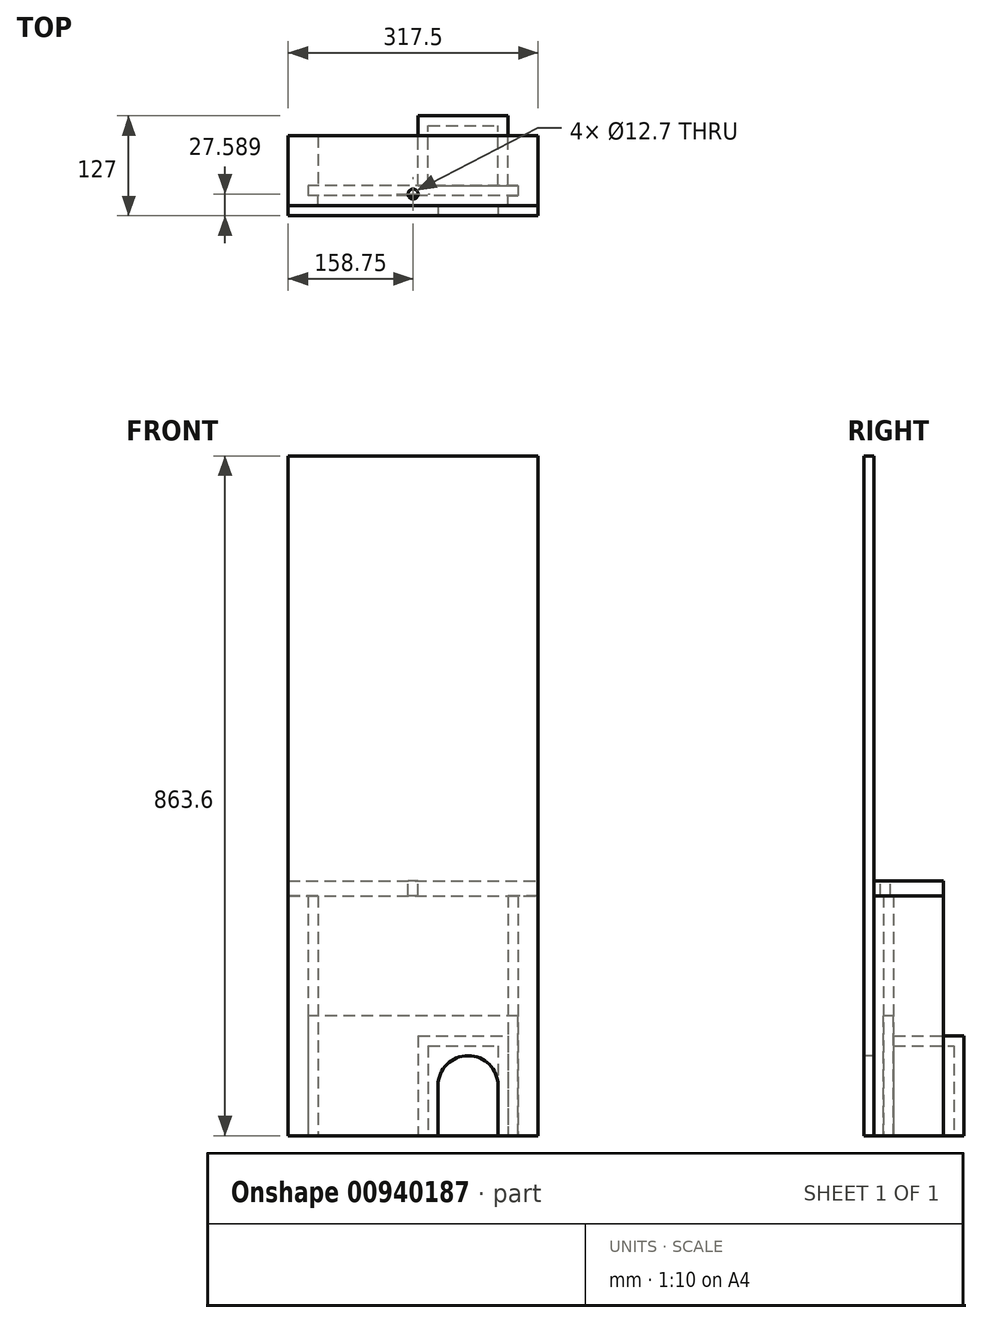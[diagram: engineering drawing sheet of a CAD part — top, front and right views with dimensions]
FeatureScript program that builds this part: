
annotation { "Feature Type Name" : "Feature", "Feature Type Description" : "" }
export const myFeature = defineFeature(function(context is Context, id is Id, definition is map)
    precondition{}
    {
        {
            var Q0;
            Q0=qCreatedBy(makeId("Front.planeOp"),FACE);
            var sketch = newSketch(context, id + "F0", { "sketchPlane" : qUnion([Q0])});
            skLineSegment(sketch, "E0.bottom", {"start": v(158.75, -431.8) * mm, "end": v(-158.75, -431.8) * mm});
            skLineSegment(sketch, "E0.top", {"start": v(158.75, 431.8) * mm, "end": v(-158.75, 431.8) * mm});
            skLineSegment(sketch, "E0.left", {"start": v(158.75, -431.8) * mm, "end": v(158.75, 431.8) * mm});
            skLineSegment(sketch, "E0.right", {"start": v(-158.75, -431.8) * mm, "end": v(-158.75, 431.8) * mm});
            skPoint(sketch, "E0.middle", {"position": v(0, 0) * mm});
            skSolve(sketch);
        }
        {
            var Q0;
            Q0 = qSketchRegion(id + "F0", true);
            extrude(context, id + "F1", {"entities" : qUnion([Q0]), "depth" : 12.7 * mm, "offsetDistance" : 25.4 * mm});
        }
        {
            var Q0;
            Q0=makeQuery(id+"F1.opExtrude","SWEPT_FACE",FACE,{"disambiguationData":[OSD([sQuery(id+"F0.wireOp",EDGE,"E0.bottom")])]});
            var sketch = newSketch(context, id + "F2", { "sketchPlane" : qUnion([Q0])});
            skLineSegment(sketch, "E1", {"start": v(-158.75, 0) * mm, "end": v(-158.75, -88.9) * mm});
            skLineSegment(sketch, "E2", {"start": v(-158.75, -88.9) * mm, "end": v(-120.65, -88.9) * mm});
            skLineSegment(sketch, "E3", {"start": v(-120.65, -88.9) * mm, "end": v(-120.65, -25.4) * mm});
            skLineSegment(sketch, "E4", {"start": v(-120.65, -25.4) * mm, "end": v(-133.35, -25.4) * mm});
            skLineSegment(sketch, "E5", {"start": v(-158.75, 0) * mm, "end": v(-120.65, 0) * mm});
            skLineSegment(sketch, "E6", {"start": v(-120.65, 0) * mm, "end": v(-120.65, -12.7) * mm});
            skLineSegment(sketch, "E7", {"start": v(-120.65, -12.7) * mm, "end": v(-133.35, -12.7) * mm});
            skLineSegment(sketch, "E8", {"start": v(-133.35, -12.7) * mm, "end": v(-133.35, -25.4) * mm});
            skLineSegment(sketch, "E9.MirrorCS", {"start": v(120.65, -25.4) * mm, "end": v(133.35, -25.4) * mm});
            skLineSegment(sketch, "E10.MirrorCS", {"start": v(120.65, -12.7) * mm, "end": v(133.35, -12.7) * mm});
            skLineSegment(sketch, "E11.MirrorCS", {"start": v(120.65, 0) * mm, "end": v(120.65, -12.7) * mm});
            skLineSegment(sketch, "E12.MirrorCS", {"start": v(120.65, -88.9) * mm, "end": v(120.65, -25.4) * mm});
            skLineSegment(sketch, "E13.MirrorCS", {"start": v(158.75, 0) * mm, "end": v(158.75, -88.9) * mm});
            skLineSegment(sketch, "E14.MirrorCS", {"start": v(158.75, 0) * mm, "end": v(120.65, 0) * mm});
            skLineSegment(sketch, "E15.MirrorCS", {"start": v(133.35, -12.7) * mm, "end": v(133.35, -25.4) * mm});
            skLineSegment(sketch, "E16.MirrorCS", {"start": v(158.75, -88.9) * mm, "end": v(120.65, -88.9) * mm});
            skSolve(sketch);
        }
        {
            var Q0;
            Q0 = qSketchRegion(id + "F2", true);
            extrude(context, id + "F3", {"entities" : qUnion([Q0]), "oppositeDirection" : true, "depth" : 304.8 * mm, "offsetDistance" : 25.4 * mm});
        }
        {
            var Q0;
            Q0=makeQuery(id+"F3.opExtrude","SWEPT_FACE",FACE,{"disambiguationData":[OSD([sQuery(id+"F2.wireOp",EDGE,"E7")])]});
            var sketch = newSketch(context, id + "F4", { "sketchPlane" : qUnion([Q0])});
            skLineSegment(sketch, "E17.bottom", {"start": v(-133.35, -431.8) * mm, "end": v(133.35, -431.8) * mm});
            skLineSegment(sketch, "E17.top", {"start": v(-133.35, -279.4) * mm, "end": v(133.35, -279.4) * mm});
            skLineSegment(sketch, "E17.left", {"start": v(-133.35, -431.8) * mm, "end": v(-133.35, -279.4) * mm});
            skLineSegment(sketch, "E17.right", {"start": v(133.35, -431.8) * mm, "end": v(133.35, -279.4) * mm});
            skSolve(sketch);
        }
        {
            var Q0;
            Q0=makeQuery(id+"F4.imprint","IMPRINT",FACE,{"disambiguationData":[TD([[makeQuery(id+"F4.imprint","IMPRINT",EDGE,{"derivedFrom":sQuery(id+"F4.wireOp",EDGE,"E17.top")}),-1.0]])]});
            extrude(context, id + "F5", {"entities" : qUnion([Q0]), "depth" : 12.7 * mm, "offsetDistance" : 25.4 * mm});
        }
        {
            var Q0;
            Q0=makeQuery(id+"F1.opExtrude","CAP_FACE",FACE,{"disambiguationData":[OSD([sQuery(id+"F0.wireOp",EDGE,"E0.bottom"),sQuery(id+"F0.wireOp",EDGE,"E0.top"),sQuery(id+"F0.wireOp",EDGE,"E0.left"),sQuery(id+"F0.wireOp",EDGE,"E0.right")])],"isStart":false});
            var sketch = newSketch(context, id + "F6", { "sketchPlane" : qUnion([Q0])});
            skLineSegment(sketch, "E18.bottom", {"start": v(31.75, -431.8) * mm, "end": v(107.95, -431.8) * mm});
            skLineSegment(sketch, "E18.left", {"start": v(31.75, -431.8) * mm, "end": v(31.75, -368.3) * mm});
            skLineSegment(sketch, "E18.right", {"start": v(107.95, -431.8) * mm, "end": v(107.95, -368.3) * mm});
            skArc(sketch, "E19", {"start": v(107.95, -368.3) * mm, "mid": v(69.85, -330.2) * mm, "end": v(31.75, -368.3) * mm});
            skSolve(sketch);
        }
        {
            var Q0;
            Q0=makeQuery(id+"F6.imprint","IMPRINT",FACE,{"disambiguationData":[TD([[makeQuery(id+"F6.imprint","IMPRINT",EDGE,{"derivedFrom":sQuery(id+"F6.wireOp",EDGE,"E18.bottom")}),-1.0]])]});
            var Q1;
            Q1=makeQuery(id+"F1.opExtrude","SWEPT_BODY",BODY,{"disambiguationData":[OSD([sQuery(id+"F0.wireOp",EDGE,"E0.bottom"),sQuery(id+"F0.wireOp",EDGE,"E0.top"),sQuery(id+"F0.wireOp",EDGE,"E0.left"),sQuery(id+"F0.wireOp",EDGE,"E0.right")])]});
            extrude(context, id + "F7", {"entities" : qUnion([Q0]), "operationType" : NewBodyOperationType.REMOVE, "oppositeDirection" : true, "depth" : 12.7 * mm, "endBoundEntityBody" : qUnion([Q1]), "offsetDistance" : 25.4 * mm});
        }
        {
            var Q0;
            Q0=makeQuery(id+"F3.opExtrude","CAP_FACE",FACE,{"disambiguationData":[OSD([sQuery(id+"F2.wireOp",EDGE,"E1"),sQuery(id+"F2.wireOp",EDGE,"E2"),sQuery(id+"F2.wireOp",EDGE,"E3"),sQuery(id+"F2.wireOp",EDGE,"E4"),sQuery(id+"F2.wireOp",EDGE,"E5"),sQuery(id+"F2.wireOp",EDGE,"E6"),sQuery(id+"F2.wireOp",EDGE,"E7"),sQuery(id+"F2.wireOp",EDGE,"E8")])],"isStart":false});
            var sketch = newSketch(context, id + "F8", { "sketchPlane" : qUnion([Q0])});
            skLineSegment(sketch, "E20.top", {"start": v(-158.75, 0) * mm, "end": v(158.75, 0) * mm});
            skLineSegment(sketch, "E20.left", {"start": v(-158.75, 88.9) * mm, "end": v(-158.75, 0) * mm});
            skLineSegment(sketch, "E21", {"start": v(-158.75, 88.9) * mm, "end": v(158.75, 88.9) * mm});
            skLineSegment(sketch, "E22", {"start": v(158.75, 88.9) * mm, "end": v(158.75, 0) * mm});
            skSolve(sketch);
        }
        {
            var Q0;
            Q0 = qSketchRegion(id + "F8", true);
            extrude(context, id + "F9", {"entities" : qUnion([Q0]), "depth" : 19.05 * mm, "offsetDistance" : 25.4 * mm});
        }
        {
            var Q0;
            Q0=makeQuery(id+"F9.opExtrude","CAP_FACE",FACE,{"disambiguationData":[OSD([sQuery(id+"F8.wireOp",EDGE,"E20.top"),sQuery(id+"F8.wireOp",EDGE,"E20.left"),sQuery(id+"F8.wireOp",EDGE,"E21"),sQuery(id+"F8.wireOp",EDGE,"E22")])],"isStart":false});
            var sketch = newSketch(context, id + "F10", { "sketchPlane" : qUnion([Q0])});
            skCircle(sketch, "E23", {"center": v(0, 14.89) * mm, "radius": 6.35 * mm});
            skPoint(sketch, "E23.centerSnap0", {"position": v(0, 88.9) * mm});
            skSolve(sketch);
        }
        {
            var Q0;
            Q0=makeQuery(id+"F10.imprint","IMPRINT",FACE,{"disambiguationData":[TD([[makeQuery(id+"F10.imprint","IMPRINT",EDGE,{"derivedFrom":sQuery(id+"F10.wireOp",EDGE,"E23")}),1.0]])]});
            extrude(context, id + "F11", {"entities" : qUnion([Q0]), "operationType" : NewBodyOperationType.REMOVE, "oppositeDirection" : true, "depth" : 25.4 * mm, "offsetDistance" : 25.4 * mm});
        }
        {
            var Q0;
            Q0=makeQuery(id+"F3.opExtrude","CAP_FACE",FACE,{"disambiguationData":[OSD([sQuery(id+"F2.wireOp",EDGE,"E9.MirrorCS"),sQuery(id+"F2.wireOp",EDGE,"E10.MirrorCS"),sQuery(id+"F2.wireOp",EDGE,"E11.MirrorCS"),sQuery(id+"F2.wireOp",EDGE,"E12.MirrorCS"),sQuery(id+"F2.wireOp",EDGE,"E13.MirrorCS"),sQuery(id+"F2.wireOp",EDGE,"E14.MirrorCS"),sQuery(id+"F2.wireOp",EDGE,"E15.MirrorCS"),sQuery(id+"F2.wireOp",EDGE,"E16.MirrorCS")])],"isStart":true});
            var sketch = newSketch(context, id + "F12", { "sketchPlane" : qUnion([Q0])});
            skLineSegment(sketch, "E24.bottom", {"start": v(6.35, -25.4) * mm, "end": v(120.65, -25.4) * mm});
            skLineSegment(sketch, "E24.top", {"start": v(6.35, -114.3) * mm, "end": v(120.65, -114.3) * mm});
            skLineSegment(sketch, "E24.left", {"start": v(6.35, -25.4) * mm, "end": v(6.35, -114.3) * mm});
            skLineSegment(sketch, "E24.right", {"start": v(120.65, -25.4) * mm, "end": v(120.65, -114.3) * mm});
            skSolve(sketch);
        }
        {
            var Q0;
            Q0=makeQuery(id+"F12.imprint","IMPRINT",FACE,{"disambiguationData":[TD([[makeQuery(id+"F12.imprint","IMPRINT",EDGE,{"derivedFrom":sQuery(id+"F12.wireOp",EDGE,"E24.bottom")}),-1.0]])]});
            extrude(context, id + "F13", {"entities" : qUnion([Q0]), "oppositeDirection" : true, "depth" : 127 * mm, "offsetDistance" : 25.4 * mm});
        }
        {
            var Q0;
            Q0=makeQuery(id+"F13.opExtrude","CAP_FACE",FACE,{"disambiguationData":[OSD([sQuery(id+"F12.wireOp",EDGE,"E24.bottom"),sQuery(id+"F12.wireOp",EDGE,"E24.top"),sQuery(id+"F12.wireOp",EDGE,"E24.left"),sQuery(id+"F12.wireOp",EDGE,"E24.right")])],"isStart":true});
            var sketch = newSketch(context, id + "F14", { "sketchPlane" : qUnion([Q0])});
            skLineSegment(sketch, "E25.bottom", {"start": v(19.05, -25.4) * mm, "end": v(107.95, -25.4) * mm});
            skLineSegment(sketch, "E25.top", {"start": v(19.05, -101.6) * mm, "end": v(107.95, -101.6) * mm});
            skLineSegment(sketch, "E25.left", {"start": v(19.05, -25.4) * mm, "end": v(19.05, -101.6) * mm});
            skLineSegment(sketch, "E25.right", {"start": v(107.95, -25.4) * mm, "end": v(107.95, -101.6) * mm});
            skSolve(sketch);
        }
        {
            var Q0;
            Q0=makeQuery(id+"F14.imprint","IMPRINT",FACE,{"disambiguationData":[TD([[makeQuery(id+"F14.imprint","IMPRINT",EDGE,{"derivedFrom":sQuery(id+"F14.wireOp",EDGE,"E25.bottom")}),-1.0]])]});
            extrude(context, id + "F15", {"entities" : qUnion([Q0]), "operationType" : NewBodyOperationType.REMOVE, "oppositeDirection" : true, "depth" : 114.3 * mm, "offsetDistance" : 25.4 * mm});
        }
    });
